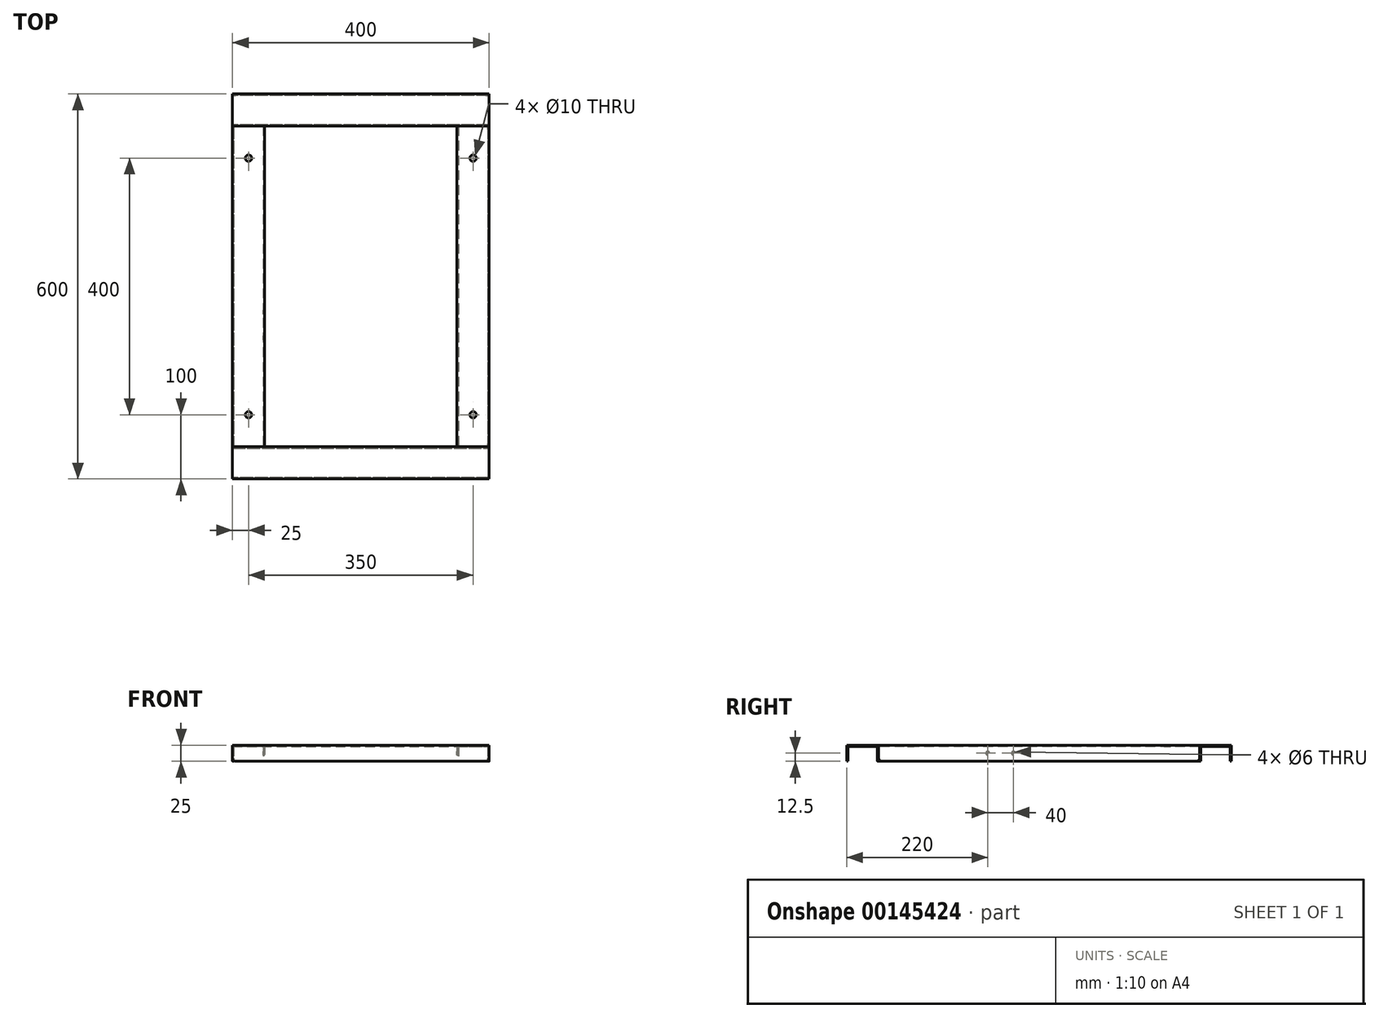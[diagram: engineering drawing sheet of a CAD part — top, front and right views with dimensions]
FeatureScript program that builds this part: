
annotation { "Feature Type Name" : "Feature", "Feature Type Description" : "" }
export const myFeature = defineFeature(function(context is Context, id is Id, definition is map)
    precondition{}
    {
        {
            var Q0;
            Q0=qCreatedBy(makeId("Top.planeOp"),FACE);
            var sketch = newSketch(context, id + "F0", { "sketchPlane" : qUnion([Q0])});
            skLineSegment(sketch, "E0.bottom", {"start": v(150, 250) * mm, "end": v(-150, 250) * mm});
            skLineSegment(sketch, "E0.top", {"start": v(150, -250) * mm, "end": v(-150, -250) * mm});
            skLineSegment(sketch, "E0.left", {"start": v(150, 250) * mm, "end": v(150, -250) * mm});
            skLineSegment(sketch, "E0.right", {"start": v(-150, 250) * mm, "end": v(-150, -250) * mm});
            skPoint(sketch, "E0.middle", {"position": v(0, 0) * mm});
            skLineSegment(sketch, "E1.0", {"start": v(200, 300) * mm, "end": v(200, -300) * mm});
            skLineSegment(sketch, "E1.1", {"start": v(200, 300) * mm, "end": v(-200, 300) * mm});
            skLineSegment(sketch, "E1.2", {"start": v(-200, 300) * mm, "end": v(-200, -300) * mm});
            skLineSegment(sketch, "E1.3", {"start": v(200, -300) * mm, "end": v(-200, -300) * mm});
            skLineSegment(sketch, "E2", {"start": v(150, 250) * mm, "end": v(200, 250) * mm});
            skLineSegment(sketch, "E3", {"start": v(-150, 250) * mm, "end": v(-200, 250) * mm});
            skLineSegment(sketch, "E4", {"start": v(-150, -250) * mm, "end": v(-200, -250) * mm});
            skLineSegment(sketch, "E5", {"start": v(150, -250) * mm, "end": v(200, -250) * mm});
            skCircle(sketch, "E6", {"center": v(175, -200) * mm, "radius": 3 * mm});
            skCircle(sketch, "E7", {"center": v(175, 200) * mm, "radius": 3 * mm});
            skCircle(sketch, "E8.MirrorC", {"center": v(-175, 200) * mm, "radius": 3 * mm});
            skCircle(sketch, "E9.MirrorC", {"center": v(-175, -200) * mm, "radius": 3 * mm});
            skSolve(sketch);
        }
        {
            var Q0;
            Q0=makeQuery(id+"F0.imprint","IMPRINT",FACE,{"disambiguationData":[TD([[makeQuery(id+"F0.imprint","IMPRINT",EDGE,{"derivedFrom":sQuery(id+"F0.wireOp",EDGE,"E0.left")}),1.0]])]});
            var Q1;
            Q1=makeQuery(id+"F0.imprint","IMPRINT",FACE,{"disambiguationData":[TD([[makeQuery(id+"F0.imprint","IMPRINT",EDGE,{"derivedFrom":sQuery(id+"F0.wireOp",EDGE,"E0.right")}),-1.0]])]});
            extrude(context, id + "F1", {"entities" : qUnion([Q0, Q1]), "depth" : 25 * mm});
        }
        {
            var Q0;
            Q0=makeQuery(id+"F0.imprint","IMPRINT",FACE,{"disambiguationData":[TD([[makeQuery(id+"F0.imprint","IMPRINT",EDGE,{"derivedFrom":sQuery(id+"F0.wireOp",EDGE,"E0.top")}),1.0]])]});
            var Q1;
            Q1=makeQuery(id+"F0.imprint","IMPRINT",FACE,{"disambiguationData":[TD([[makeQuery(id+"F0.imprint","IMPRINT",EDGE,{"derivedFrom":sQuery(id+"F0.wireOp",EDGE,"E0.bottom")}),-1.0]])]});
            extrude(context, id + "F2", {"entities" : qUnion([Q0, Q1]), "depth" : 25 * mm});
        }
        {
            var Q0;
            Q0=makeQuery(id+"F2.opExtrude","CAP_FACE",FACE,{"disambiguationData":[OSD([sQuery(id+"F0.wireOp",EDGE,"E0.top"),sQuery(id+"F0.wireOp",EDGE,"E1.0"),sQuery(id+"F0.wireOp",EDGE,"E1.2"),sQuery(id+"F0.wireOp",EDGE,"E1.3"),sQuery(id+"F0.wireOp",EDGE,"E4"),sQuery(id+"F0.wireOp",EDGE,"E5")])],"isStart":true});
            var Q1;
            {var subQ0=sQuery(id+"F0.wireOp",EDGE,"E1.0");Q1=makeQuery(id+"F2.opExtrude","SWEPT_FACE",FACE,{"disambiguationData":[OSD([subQ0]),TDD([makeQuery(id+"F0.imprint","IMPRINT",EDGE,{"disambiguationData":[TD([[makeQuery(id+"F0.imprint","INTERSECT",VERTEX,{"derivedFrom":[subQ0,sQuery(id+"F0.wireOp",EDGE,"E1.3")]}),1.0]])],"derivedFrom":subQ0})])]});}
            var Q2;
            {var subQ0=sQuery(id+"F0.wireOp",EDGE,"E1.2");Q2=makeQuery(id+"F2.opExtrude","SWEPT_FACE",FACE,{"disambiguationData":[OSD([subQ0]),TDD([makeQuery(id+"F0.imprint","IMPRINT",EDGE,{"disambiguationData":[TD([[makeQuery(id+"F0.imprint","INTERSECT",VERTEX,{"derivedFrom":[subQ0,sQuery(id+"F0.wireOp",EDGE,"E1.3")]}),1.0]])],"derivedFrom":subQ0})])]});}
            var Q3;
            Q3=makeQuery(id+"F1.opExtrude","CAP_FACE",FACE,{"disambiguationData":[OSD([sQuery(id+"F0.wireOp",EDGE,"E0.left"),sQuery(id+"F0.wireOp",EDGE,"E1.0"),sQuery(id+"F0.wireOp",EDGE,"E2"),sQuery(id+"F0.wireOp",EDGE,"E5")])],"isStart":true});
            var Q4;
            Q4=makeQuery(id+"F1.opExtrude","SWEPT_FACE",FACE,{"disambiguationData":[OSD([sQuery(id+"F0.wireOp",EDGE,"E5")])]});
            var Q5;
            Q5=makeQuery(id+"F2.opExtrude","CAP_FACE",FACE,{"disambiguationData":[OSD([sQuery(id+"F0.wireOp",EDGE,"E0.bottom"),sQuery(id+"F0.wireOp",EDGE,"E1.0"),sQuery(id+"F0.wireOp",EDGE,"E1.1"),sQuery(id+"F0.wireOp",EDGE,"E1.2"),sQuery(id+"F0.wireOp",EDGE,"E2"),sQuery(id+"F0.wireOp",EDGE,"E3")])],"isStart":true});
            var Q6;
            {var subQ0=sQuery(id+"F0.wireOp",EDGE,"E1.0");Q6=makeQuery(id+"F2.opExtrude","SWEPT_FACE",FACE,{"disambiguationData":[OSD([subQ0]),TDD([makeQuery(id+"F0.imprint","IMPRINT",EDGE,{"disambiguationData":[TD([[makeQuery(id+"F0.imprint","INTERSECT",VERTEX,{"derivedFrom":[subQ0,sQuery(id+"F0.wireOp",EDGE,"E1.1")]}),-1.0]])],"derivedFrom":subQ0})])]});}
            var Q7;
            Q7=makeQuery(id+"F1.opExtrude","CAP_FACE",FACE,{"disambiguationData":[OSD([sQuery(id+"F0.wireOp",EDGE,"E0.right"),sQuery(id+"F0.wireOp",EDGE,"E1.2"),sQuery(id+"F0.wireOp",EDGE,"E3"),sQuery(id+"F0.wireOp",EDGE,"E4")])],"isStart":true});
            var Q8;
            Q8=makeQuery(id+"F1.opExtrude","SWEPT_FACE",FACE,{"disambiguationData":[OSD([sQuery(id+"F0.wireOp",EDGE,"E4")])]});
            var Q9;
            Q9=makeQuery(id+"F1.opExtrude","SWEPT_FACE",FACE,{"disambiguationData":[OSD([sQuery(id+"F0.wireOp",EDGE,"E3")])]});
            var Q10;
            Q10=makeQuery(id+"F1.opExtrude","SWEPT_FACE",FACE,{"disambiguationData":[OSD([sQuery(id+"F0.wireOp",EDGE,"E2")])]});
            var Q11;
            {var subQ0=sQuery(id+"F0.wireOp",EDGE,"E1.2");Q11=makeQuery(id+"F2.opExtrude","SWEPT_FACE",FACE,{"disambiguationData":[OSD([subQ0]),TDD([makeQuery(id+"F0.imprint","IMPRINT",EDGE,{"disambiguationData":[TD([[makeQuery(id+"F0.imprint","INTERSECT",VERTEX,{"derivedFrom":[sQuery(id+"F0.wireOp",EDGE,"E1.1"),subQ0]}),-1.0]])],"derivedFrom":subQ0})])]});}
            shell(context, id + "F3", {"entities" : qUnion([Q0, Q1, Q2, Q3, Q4, Q5, Q6, Q7, Q8, Q9, Q10, Q11]), "thickness" : 2 * mm});
        }
        {
            var Q0;
            {var subQ0=sQuery(id+"F0.wireOp",EDGE,"E1.2");Q0=makeQuery(id+"F2.opExtrude","CAP_EDGE",EDGE,{"disambiguationData":[OSD([subQ0]),TDD([makeQuery(id+"F0.imprint","IMPRINT",EDGE,{"disambiguationData":[TD([[makeQuery(id+"F0.imprint","INTERSECT",VERTEX,{"derivedFrom":[sQuery(id+"F0.wireOp",EDGE,"E1.1"),subQ0]}),-1.0]])],"derivedFrom":subQ0})])],"isStart":true});}
            var Q1;
            {var subQ0=sQuery(id+"F0.wireOp",EDGE,"E1.0");Q1=makeQuery(id+"F2.opExtrude","CAP_EDGE",EDGE,{"disambiguationData":[OSD([subQ0]),TDD([makeQuery(id+"F0.imprint","IMPRINT",EDGE,{"disambiguationData":[TD([[makeQuery(id+"F0.imprint","INTERSECT",VERTEX,{"derivedFrom":[subQ0,sQuery(id+"F0.wireOp",EDGE,"E1.1")]}),-1.0]])],"derivedFrom":subQ0})])],"isStart":true});}
            var Q2;
            {var subQ0=sQuery(id+"F0.wireOp",EDGE,"E1.0");Q2=makeQuery(id+"F3.opShell","OFFSET_EDGE",EDGE,{"disambiguationData":[OSD([subQ0]),TDD([makeQuery(id+"F2.opExtrude","CAP_EDGE",EDGE,{"disambiguationData":[OSD([subQ0]),TDD([makeQuery(id+"F0.imprint","IMPRINT",EDGE,{"disambiguationData":[TD([[makeQuery(id+"F0.imprint","INTERSECT",VERTEX,{"derivedFrom":[subQ0,sQuery(id+"F0.wireOp",EDGE,"E1.1")]}),-1.0]])],"derivedFrom":subQ0})])],"isStart":true})])]});}
            var Q3;
            {var subQ0=sQuery(id+"F0.wireOp",EDGE,"E2");Q3=makeQuery(id+"F3.opShell","OFFSET_EDGE",EDGE,{"disambiguationData":[OSD([subQ0]),TDD([makeQuery(id+"F1.opExtrude","CAP_EDGE",EDGE,{"disambiguationData":[OSD([subQ0])],"isStart":true})])]});}
            var Q4;
            {var subQ0=sQuery(id+"F0.wireOp",EDGE,"E1.2");Q4=makeQuery(id+"F3.opShell","OFFSET_EDGE",EDGE,{"disambiguationData":[OSD([subQ0]),TDD([makeQuery(id+"F2.opExtrude","CAP_EDGE",EDGE,{"disambiguationData":[OSD([subQ0]),TDD([makeQuery(id+"F0.imprint","IMPRINT",EDGE,{"disambiguationData":[TD([[makeQuery(id+"F0.imprint","INTERSECT",VERTEX,{"derivedFrom":[sQuery(id+"F0.wireOp",EDGE,"E1.1"),subQ0]}),-1.0]])],"derivedFrom":subQ0})])],"isStart":true})])]});}
            var Q5;
            {var subQ0=sQuery(id+"F0.wireOp",EDGE,"E3");Q5=makeQuery(id+"F3.opShell","OFFSET_EDGE",EDGE,{"disambiguationData":[OSD([subQ0]),TDD([makeQuery(id+"F1.opExtrude","CAP_EDGE",EDGE,{"disambiguationData":[OSD([subQ0])],"isStart":true})])]});}
            var Q6;
            {var subQ0=sQuery(id+"F0.wireOp",EDGE,"E1.2");Q6=makeQuery(id+"F2.opExtrude","CAP_EDGE",EDGE,{"disambiguationData":[OSD([subQ0]),TDD([makeQuery(id+"F0.imprint","IMPRINT",EDGE,{"disambiguationData":[TD([[makeQuery(id+"F0.imprint","INTERSECT",VERTEX,{"derivedFrom":[subQ0,sQuery(id+"F0.wireOp",EDGE,"E1.3")]}),1.0]])],"derivedFrom":subQ0})])],"isStart":true});}
            var Q7;
            {var subQ0=sQuery(id+"F0.wireOp",EDGE,"E1.2");Q7=makeQuery(id+"F3.opShell","OFFSET_EDGE",EDGE,{"disambiguationData":[OSD([subQ0]),TDD([makeQuery(id+"F2.opExtrude","CAP_EDGE",EDGE,{"disambiguationData":[OSD([subQ0]),TDD([makeQuery(id+"F0.imprint","IMPRINT",EDGE,{"disambiguationData":[TD([[makeQuery(id+"F0.imprint","INTERSECT",VERTEX,{"derivedFrom":[subQ0,sQuery(id+"F0.wireOp",EDGE,"E1.3")]}),1.0]])],"derivedFrom":subQ0})])],"isStart":true})])]});}
            var Q8;
            {var subQ0=sQuery(id+"F0.wireOp",EDGE,"E4");Q8=makeQuery(id+"F3.opShell","OFFSET_EDGE",EDGE,{"disambiguationData":[OSD([subQ0]),TDD([makeQuery(id+"F1.opExtrude","CAP_EDGE",EDGE,{"disambiguationData":[OSD([subQ0])],"isStart":true})])]});}
            var Q9;
            {var subQ0=sQuery(id+"F0.wireOp",EDGE,"E1.0");Q9=makeQuery(id+"F3.opShell","OFFSET_EDGE",EDGE,{"disambiguationData":[OSD([subQ0]),TDD([makeQuery(id+"F2.opExtrude","CAP_EDGE",EDGE,{"disambiguationData":[OSD([subQ0]),TDD([makeQuery(id+"F0.imprint","IMPRINT",EDGE,{"disambiguationData":[TD([[makeQuery(id+"F0.imprint","INTERSECT",VERTEX,{"derivedFrom":[subQ0,sQuery(id+"F0.wireOp",EDGE,"E1.3")]}),1.0]])],"derivedFrom":subQ0})])],"isStart":true})])]});}
            var Q10;
            {var subQ0=sQuery(id+"F0.wireOp",EDGE,"E1.0");Q10=makeQuery(id+"F2.opExtrude","CAP_EDGE",EDGE,{"disambiguationData":[OSD([subQ0]),TDD([makeQuery(id+"F0.imprint","IMPRINT",EDGE,{"disambiguationData":[TD([[makeQuery(id+"F0.imprint","INTERSECT",VERTEX,{"derivedFrom":[subQ0,sQuery(id+"F0.wireOp",EDGE,"E1.3")]}),1.0]])],"derivedFrom":subQ0})])],"isStart":true});}
            var Q11;
            {var subQ0=sQuery(id+"F0.wireOp",EDGE,"E5");Q11=makeQuery(id+"F3.opShell","OFFSET_EDGE",EDGE,{"disambiguationData":[OSD([subQ0]),TDD([makeQuery(id+"F1.opExtrude","CAP_EDGE",EDGE,{"disambiguationData":[OSD([subQ0])],"isStart":true})])]});}
            fillet(context, id + "F4", {"entities" : qUnion([Q0, Q1, Q2, Q3, Q4, Q5, Q6, Q7, Q8, Q9, Q10, Q11]), "radius" : 5 * mm, "tangentPropagation" : true, "allowEdgeOverflow" : false});
        }
        {
            var Q0;
            Q0=makeQuery(id+"F3.opShell","OFFSET_FACE",FACE,{"disambiguationData":[OSD([sQuery(id+"F0.wireOp",EDGE,"E0.left")])]});
            var sketch = newSketch(context, id + "F5", { "sketchPlane" : qUnion([Q0])});
            skCircle(sketch, "E10", {"center": v(-80, 12.5) * mm, "radius": 3 * mm});
            skCircle(sketch, "E11", {"center": v(-40, 12.5) * mm, "radius": 3 * mm});
            skSolve(sketch);
        }
        {
            var Q0;
            Q0 = qSketchRegion(id + "F5", true);
            extrude(context, id + "F6", {"entities" : qUnion([Q0]), "operationType" : NewBodyOperationType.REMOVE, "oppositeDirection" : true, "depth" : 325 * mm});
        }
        {
            var Q0;
            {var subQ0=sQuery(id+"F0.wireOp",EDGE,"E9.MirrorC");var subQ1=sQuery(id+"F0.wireOp",EDGE,"E8.MirrorC");var subQ2=sQuery(id+"F0.wireOp",EDGE,"E4");var subQ3=sQuery(id+"F0.wireOp",EDGE,"E3");var subQ4=sQuery(id+"F0.wireOp",EDGE,"E1.2");var subQ5=sQuery(id+"F0.wireOp",EDGE,"E0.right");Q0=makeQuery(id+"F3.opShell","OFFSET_FACE",FACE,{"disambiguationData":[OSD([subQ5,subQ4,subQ3,subQ2,subQ1,subQ0]),TDD([makeQuery(id+"F1.opExtrude","CAP_FACE",FACE,{"disambiguationData":[OSD([subQ5,subQ4,subQ3,subQ2,subQ1,subQ0])],"isStart":true})]),OD(2.0)]});}
            var Q1;
            {var subQ0=sQuery(id+"F0.wireOp",EDGE,"E7");var subQ1=sQuery(id+"F0.wireOp",EDGE,"E6");var subQ2=sQuery(id+"F0.wireOp",EDGE,"E5");var subQ3=sQuery(id+"F0.wireOp",EDGE,"E2");var subQ4=sQuery(id+"F0.wireOp",EDGE,"E1.0");var subQ5=sQuery(id+"F0.wireOp",EDGE,"E0.left");Q1=makeQuery(id+"F3.opShell","OFFSET_FACE",FACE,{"disambiguationData":[OSD([subQ5,subQ4,subQ3,subQ2,subQ1,subQ0]),TDD([makeQuery(id+"F1.opExtrude","CAP_FACE",FACE,{"disambiguationData":[OSD([subQ5,subQ4,subQ3,subQ2,subQ1,subQ0])],"isStart":true})]),OD(1.0)]});}
            var Q2;
            {var subQ0=sQuery(id+"F0.wireOp",EDGE,"E7");var subQ1=sQuery(id+"F0.wireOp",EDGE,"E6");var subQ2=sQuery(id+"F0.wireOp",EDGE,"E5");var subQ3=sQuery(id+"F0.wireOp",EDGE,"E2");var subQ4=sQuery(id+"F0.wireOp",EDGE,"E1.0");var subQ5=sQuery(id+"F0.wireOp",EDGE,"E0.left");Q2=makeQuery(id+"F3.opShell","OFFSET_FACE",FACE,{"disambiguationData":[OSD([subQ5,subQ4,subQ3,subQ2,subQ1,subQ0]),TDD([makeQuery(id+"F1.opExtrude","CAP_FACE",FACE,{"disambiguationData":[OSD([subQ5,subQ4,subQ3,subQ2,subQ1,subQ0])],"isStart":true})]),OD(2.0)]});}
            var Q3;
            {var subQ0=sQuery(id+"F0.wireOp",EDGE,"E9.MirrorC");var subQ1=sQuery(id+"F0.wireOp",EDGE,"E8.MirrorC");var subQ2=sQuery(id+"F0.wireOp",EDGE,"E4");var subQ3=sQuery(id+"F0.wireOp",EDGE,"E3");var subQ4=sQuery(id+"F0.wireOp",EDGE,"E1.2");var subQ5=sQuery(id+"F0.wireOp",EDGE,"E0.right");Q3=makeQuery(id+"F3.opShell","OFFSET_FACE",FACE,{"disambiguationData":[OSD([subQ5,subQ4,subQ3,subQ2,subQ1,subQ0]),TDD([makeQuery(id+"F1.opExtrude","CAP_FACE",FACE,{"disambiguationData":[OSD([subQ5,subQ4,subQ3,subQ2,subQ1,subQ0])],"isStart":true})]),OD(1.0)]});}
            extrude(context, id + "F7", {"entities" : qUnion([Q0, Q1, Q2, Q3]), "operationType" : NewBodyOperationType.REMOVE, "oppositeDirection" : true, "depth" : 25 * mm});
        }
    });
